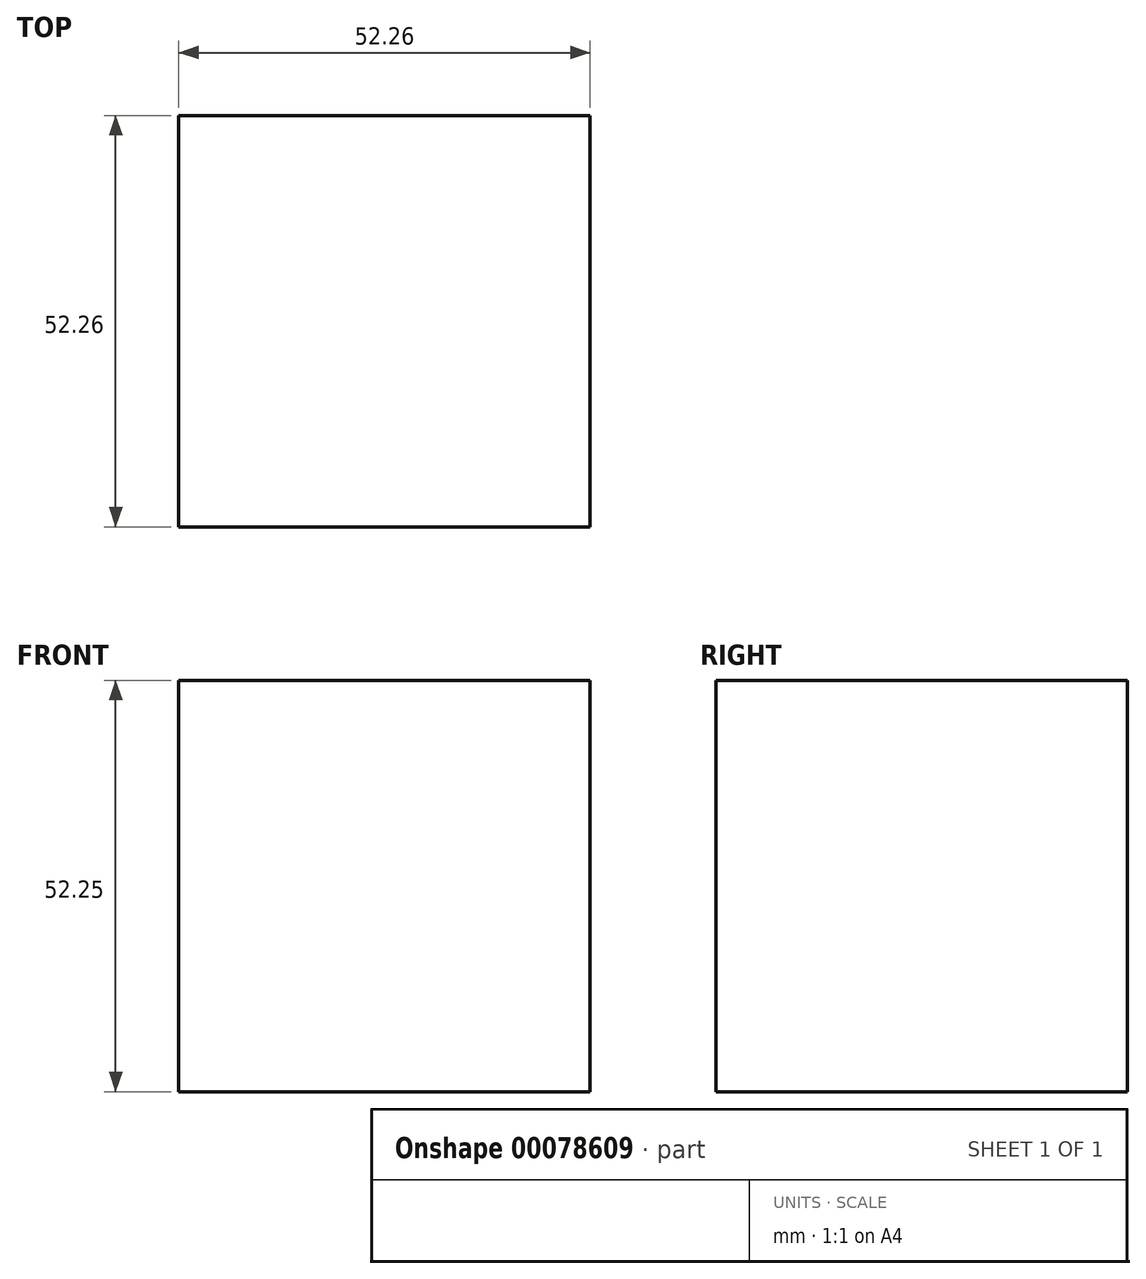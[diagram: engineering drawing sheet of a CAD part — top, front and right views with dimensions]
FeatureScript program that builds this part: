
annotation { "Feature Type Name" : "Feature", "Feature Type Description" : "" }
export const myFeature = defineFeature(function(context is Context, id is Id, definition is map)
    precondition{}
    {
        {
            var Q0;
            Q0=qCreatedBy(makeId("Top.planeOp"),FACE);
            var sketch = newSketch(context, id + "F0", { "sketchPlane" : qUnion([Q0])});
            skLineSegment(sketch, "E0.bottom", {"start": v(0, 0) * mm, "end": v(52.26, 0) * mm});
            skLineSegment(sketch, "E0.top", {"start": v(0, 52.26) * mm, "end": v(52.26, 52.26) * mm});
            skLineSegment(sketch, "E0.left", {"start": v(0, 0) * mm, "end": v(0, 52.26) * mm});
            skLineSegment(sketch, "E0.right", {"start": v(52.26, 0) * mm, "end": v(52.26, 52.26) * mm});
            skSolve(sketch);
        }
        {
            var Q0;
            Q0=makeQuery(id+"F0.imprint","IMPRINT",FACE,{"disambiguationData":[TD([[makeQuery(id+"F0.imprint","IMPRINT",EDGE,{"derivedFrom":sQuery(id+"F0.wireOp",EDGE,"E0.bottom")}),1.0]])]});
            extrude(context, id + "F1", {"entities" : qUnion([Q0]), "depth" : 52.25 * mm});
        }
    });
